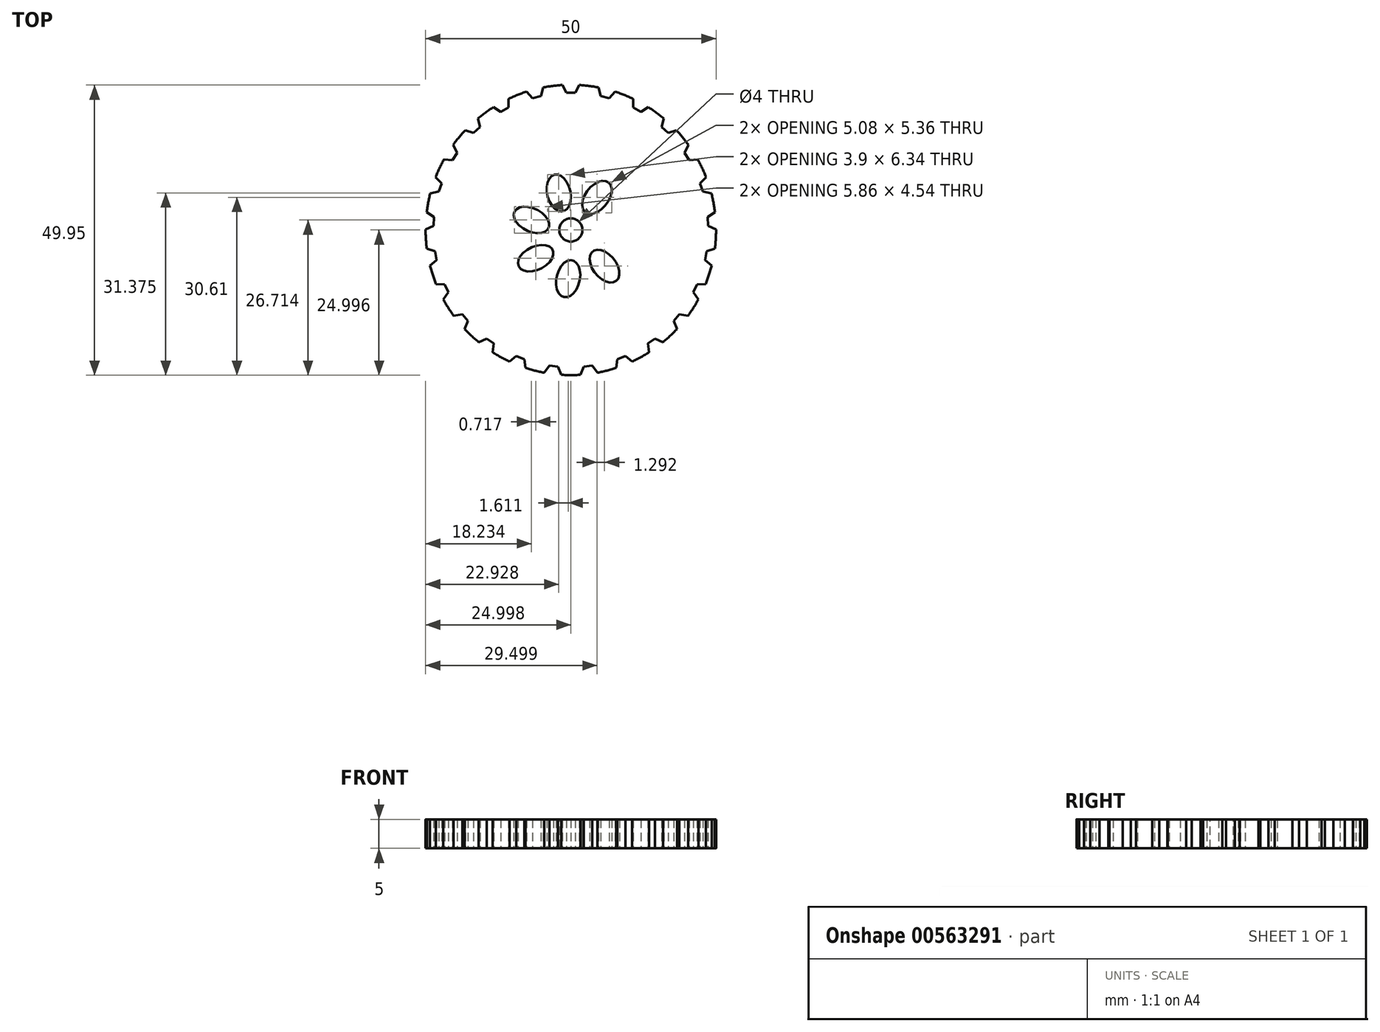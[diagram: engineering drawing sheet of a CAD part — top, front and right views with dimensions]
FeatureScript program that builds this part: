
annotation { "Feature Type Name" : "Feature", "Feature Type Description" : "" }
export const myFeature = defineFeature(function(context is Context, id is Id, definition is map)
    precondition{}
    {
        {
            var Q0;
            Q0=qCreatedBy(makeId("Top.planeOp"),FACE);
            var sketch = newSketch(context, id + "F0", { "sketchPlane" : qUnion([Q0])});
            skArc(sketch, "E0", {"start": v(-18.7, -16.22) * mm, "mid": v(-17.54, -17.4) * mm, "end": v(-16.29, -18.5) * mm});
            skPoint(sketch, "E1.center", {"position": v(0, 0) * mm});
            skArc(sketch, "E2", {"start": v(-8.06, 24.63) * mm, "mid": v(-9.62, 24.07) * mm, "end": v(-11.15, 23.4) * mm});
            skLineSegment(sketch, "E3", {"start": v(-1.9, 25.78) * mm, "end": v(-1.17, 24.47) * mm});
            skLineSegment(sketch, "E4", {"start": v(-1.17, 24.47) * mm, "end": v(0.33, 24.47) * mm});
            skLineSegment(sketch, "E5", {"start": v(0.33, 24.47) * mm, "end": v(1.06, 25.78) * mm});
            skLineSegment(sketch, "E6.1.0", {"start": v(-8.06, 24.63) * mm, "end": v(-7.03, 23.54) * mm});
            skLineSegment(sketch, "E6.1.1", {"start": v(-7.03, 23.54) * mm, "end": v(-5.58, 23.91) * mm});
            skLineSegment(sketch, "E6.1.2", {"start": v(-5.58, 23.91) * mm, "end": v(-5.2, 25.37) * mm});
            skLineSegment(sketch, "E6.2.0", {"start": v(-13.74, 21.98) * mm, "end": v(-12.47, 21.18) * mm});
            skLineSegment(sketch, "E6.2.1", {"start": v(-12.47, 21.18) * mm, "end": v(-11.16, 21.9) * mm});
            skLineSegment(sketch, "E6.2.2", {"start": v(-11.16, 21.9) * mm, "end": v(-11.15, 23.4) * mm});
            skLineSegment(sketch, "E7.2.3.0", {"start": v(-18.58, 18) * mm, "end": v(-17.15, 17.55) * mm});
            skLineSegment(sketch, "E7.3.3.0", {"start": v(-17.15, 17.55) * mm, "end": v(-16.06, 18.58) * mm});
            skLineSegment(sketch, "E7.6.3.0", {"start": v(-16.06, 18.58) * mm, "end": v(-16.43, 20.03) * mm});
            skLineSegment(sketch, "E7.2.4.0", {"start": v(-22.28, 12.95) * mm, "end": v(-20.79, 12.86) * mm});
            skLineSegment(sketch, "E7.3.4.0", {"start": v(-20.79, 12.86) * mm, "end": v(-19.98, 14.13) * mm});
            skLineSegment(sketch, "E7.6.4.0", {"start": v(-19.98, 14.13) * mm, "end": v(-20.7, 15.45) * mm});
            skLineSegment(sketch, "E7.2.5.0", {"start": v(-24.61, 7.13) * mm, "end": v(-23.14, 7.42) * mm});
            skLineSegment(sketch, "E7.3.5.0", {"start": v(-23.14, 7.42) * mm, "end": v(-22.68, 8.85) * mm});
            skLineSegment(sketch, "E7.6.5.0", {"start": v(-22.68, 8.85) * mm, "end": v(-23.7, 9.94) * mm});
            skLineSegment(sketch, "E7.2.6.0", {"start": v(-25.42, 0.92) * mm, "end": v(-24.07, 1.56) * mm});
            skLineSegment(sketch, "E7.3.6.0", {"start": v(-24.07, 1.56) * mm, "end": v(-23.97, 3.06) * mm});
            skLineSegment(sketch, "E7.6.6.0", {"start": v(-23.97, 3.06) * mm, "end": v(-25.24, 3.87) * mm});
            skLineSegment(sketch, "E7.2.7.0", {"start": v(-24.66, -5.3) * mm, "end": v(-23.5, -4.34) * mm});
            skLineSegment(sketch, "E7.3.7.0", {"start": v(-23.5, -4.34) * mm, "end": v(-23.79, -2.87) * mm});
            skLineSegment(sketch, "E7.6.7.0", {"start": v(-23.79, -2.87) * mm, "end": v(-25.21, -2.4) * mm});
            skLineSegment(sketch, "E7.2.8.0", {"start": v(-22.37, -11.14) * mm, "end": v(-21.5, -9.92) * mm});
            skLineSegment(sketch, "E7.3.8.0", {"start": v(-21.5, -9.92) * mm, "end": v(-22.13, -8.56) * mm});
            skLineSegment(sketch, "E7.6.8.0", {"start": v(-22.13, -8.56) * mm, "end": v(-23.63, -8.46) * mm});
            skLineSegment(sketch, "E7.2.9.0", {"start": v(-18.7, -16.22) * mm, "end": v(-18.16, -14.82) * mm});
            skLineSegment(sketch, "E7.3.9.0", {"start": v(-18.16, -14.82) * mm, "end": v(-19.12, -13.67) * mm});
            skLineSegment(sketch, "E7.6.9.0", {"start": v(-19.12, -13.67) * mm, "end": v(-20.6, -13.94) * mm});
            skLineSegment(sketch, "E7.2.10.0", {"start": v(-13.9, -20.23) * mm, "end": v(-13.71, -18.74) * mm});
            skLineSegment(sketch, "E7.3.10.0", {"start": v(-13.71, -18.74) * mm, "end": v(-14.93, -17.86) * mm});
            skLineSegment(sketch, "E7.6.10.0", {"start": v(-14.93, -17.86) * mm, "end": v(-16.29, -18.5) * mm});
            skLineSegment(sketch, "E7.2.11.0", {"start": v(-8.24, -22.92) * mm, "end": v(-8.43, -21.43) * mm});
            skLineSegment(sketch, "E7.3.11.0", {"start": v(-8.43, -21.43) * mm, "end": v(-9.82, -20.88) * mm});
            skLineSegment(sketch, "E7.6.11.0", {"start": v(-9.82, -20.88) * mm, "end": v(-10.98, -21.83) * mm});
            skLineSegment(sketch, "E7.2.12.0", {"start": v(-2.08, -24.12) * mm, "end": v(-2.64, -22.73) * mm});
            skLineSegment(sketch, "E7.3.12.0", {"start": v(-2.64, -22.73) * mm, "end": v(-4.13, -22.54) * mm});
            skLineSegment(sketch, "E7.6.12.0", {"start": v(-4.13, -22.54) * mm, "end": v(-5.01, -23.75) * mm});
            skLineSegment(sketch, "E7.2.13.0", {"start": v(4.17, -23.75) * mm, "end": v(3.29, -22.54) * mm});
            skLineSegment(sketch, "E7.3.13.0", {"start": v(3.29, -22.54) * mm, "end": v(1.8, -22.73) * mm});
            skLineSegment(sketch, "E7.6.13.0", {"start": v(1.8, -22.73) * mm, "end": v(1.24, -24.12) * mm});
            skLineSegment(sketch, "E7.2.14.0", {"start": v(10.14, -21.83) * mm, "end": v(8.98, -20.88) * mm});
            skLineSegment(sketch, "E7.3.14.0", {"start": v(8.98, -20.88) * mm, "end": v(7.59, -21.43) * mm});
            skLineSegment(sketch, "E7.6.14.0", {"start": v(7.59, -21.43) * mm, "end": v(7.4, -22.92) * mm});
            skLineSegment(sketch, "E7.2.15.0", {"start": v(15.44, -18.5) * mm, "end": v(14.08, -17.86) * mm});
            skLineSegment(sketch, "E7.3.15.0", {"start": v(14.08, -17.86) * mm, "end": v(12.87, -18.74) * mm});
            skLineSegment(sketch, "E7.6.15.0", {"start": v(12.87, -18.74) * mm, "end": v(13.05, -20.23) * mm});
            skLineSegment(sketch, "E7.2.16.0", {"start": v(19.75, -13.94) * mm, "end": v(18.27, -13.67) * mm});
            skLineSegment(sketch, "E7.3.16.0", {"start": v(18.27, -13.67) * mm, "end": v(17.32, -14.82) * mm});
            skLineSegment(sketch, "E7.6.16.0", {"start": v(17.32, -14.82) * mm, "end": v(17.87, -16.22) * mm});
            skLineSegment(sketch, "E7.2.17.0", {"start": v(22.79, -8.46) * mm, "end": v(21.3, -8.56) * mm});
            skLineSegment(sketch, "E7.3.17.0", {"start": v(21.3, -8.56) * mm, "end": v(20.65, -9.92) * mm});
            skLineSegment(sketch, "E7.6.17.0", {"start": v(20.65, -9.92) * mm, "end": v(21.53, -11.14) * mm});
            skLineSegment(sketch, "E7.2.18.0", {"start": v(24.37, -2.4) * mm, "end": v(22.94, -2.87) * mm});
            skLineSegment(sketch, "E7.3.18.0", {"start": v(22.94, -2.87) * mm, "end": v(22.66, -4.34) * mm});
            skLineSegment(sketch, "E7.6.18.0", {"start": v(22.66, -4.34) * mm, "end": v(23.82, -5.3) * mm});
            skLineSegment(sketch, "E7.2.19.0", {"start": v(24.4, 3.87) * mm, "end": v(23.13, 3.06) * mm});
            skLineSegment(sketch, "E7.3.19.0", {"start": v(23.13, 3.06) * mm, "end": v(23.22, 1.56) * mm});
            skLineSegment(sketch, "E7.6.19.0", {"start": v(23.22, 1.56) * mm, "end": v(24.58, 0.92) * mm});
            skLineSegment(sketch, "E7.2.20.0", {"start": v(22.86, 9.94) * mm, "end": v(21.83, 8.85) * mm});
            skLineSegment(sketch, "E7.3.20.0", {"start": v(21.83, 8.85) * mm, "end": v(22.3, 7.42) * mm});
            skLineSegment(sketch, "E7.6.20.0", {"start": v(22.3, 7.42) * mm, "end": v(23.77, 7.13) * mm});
            skLineSegment(sketch, "E7.2.21.0", {"start": v(19.86, 15.45) * mm, "end": v(19.14, 14.13) * mm});
            skLineSegment(sketch, "E7.3.21.0", {"start": v(19.14, 14.13) * mm, "end": v(19.94, 12.86) * mm});
            skLineSegment(sketch, "E7.6.21.0", {"start": v(19.94, 12.86) * mm, "end": v(21.44, 12.95) * mm});
            skLineSegment(sketch, "E7.2.22.0", {"start": v(15.59, 20.03) * mm, "end": v(15.22, 18.58) * mm});
            skLineSegment(sketch, "E7.3.22.0", {"start": v(15.22, 18.58) * mm, "end": v(16.31, 17.55) * mm});
            skLineSegment(sketch, "E7.6.22.0", {"start": v(16.31, 17.55) * mm, "end": v(17.74, 18) * mm});
            skLineSegment(sketch, "E7.2.23.0", {"start": v(10.3, 23.4) * mm, "end": v(10.31, 21.9) * mm});
            skLineSegment(sketch, "E7.3.23.0", {"start": v(10.31, 21.9) * mm, "end": v(11.63, 21.18) * mm});
            skLineSegment(sketch, "E7.6.23.0", {"start": v(11.63, 21.18) * mm, "end": v(12.9, 21.98) * mm});
            skLineSegment(sketch, "E7.2.24.0", {"start": v(4.35, 25.37) * mm, "end": v(4.73, 23.91) * mm});
            skLineSegment(sketch, "E7.3.24.0", {"start": v(4.73, 23.91) * mm, "end": v(6.19, 23.54) * mm});
            skLineSegment(sketch, "E7.6.24.0", {"start": v(6.19, 23.54) * mm, "end": v(7.22, 24.63) * mm});
            skArc(sketch, "E8.trimOffspring", {"start": v(-1.9, 25.78) * mm, "mid": v(-3.55, 25.63) * mm, "end": v(-5.2, 25.37) * mm});
            skArc(sketch, "E9.trimOffspring", {"start": v(4.35, 25.37) * mm, "mid": v(2.71, 25.63) * mm, "end": v(1.06, 25.78) * mm});
            skArc(sketch, "E10.trimOffspring", {"start": v(10.3, 23.4) * mm, "mid": v(8.78, 24.07) * mm, "end": v(7.22, 24.63) * mm});
            skArc(sketch, "E11.trimOffspring", {"start": v(15.59, 20.03) * mm, "mid": v(14.27, 21.05) * mm, "end": v(12.9, 21.98) * mm});
            skArc(sketch, "E12.trimOffspring", {"start": v(19.86, 15.45) * mm, "mid": v(18.84, 16.76) * mm, "end": v(17.74, 18) * mm});
            skArc(sketch, "E13.trimOffspring", {"start": v(22.86, 9.94) * mm, "mid": v(22.2, 11.47) * mm, "end": v(21.44, 12.95) * mm});
            skArc(sketch, "E14.trimOffspring", {"start": v(24.4, 3.87) * mm, "mid": v(24.14, 5.51) * mm, "end": v(23.77, 7.13) * mm});
            skArc(sketch, "E15.trimOffspring", {"start": v(24.37, -2.4) * mm, "mid": v(24.53, -0.74) * mm, "end": v(24.58, 0.92) * mm});
            skArc(sketch, "E16.trimOffspring", {"start": v(22.79, -8.46) * mm, "mid": v(23.35, -6.9) * mm, "end": v(23.82, -5.3) * mm});
            skArc(sketch, "E17.trimOffspring", {"start": v(19.75, -13.94) * mm, "mid": v(20.69, -12.57) * mm, "end": v(21.53, -11.14) * mm});
            skArc(sketch, "E18.trimOffspring", {"start": v(15.44, -18.5) * mm, "mid": v(16.7, -17.4) * mm, "end": v(17.87, -16.22) * mm});
            skArc(sketch, "E19.trimOffspring", {"start": v(10.14, -21.83) * mm, "mid": v(11.62, -21.08) * mm, "end": v(13.05, -20.23) * mm});
            skArc(sketch, "E20.trimOffspring", {"start": v(4.17, -23.75) * mm, "mid": v(5.8, -23.39) * mm, "end": v(7.4, -22.92) * mm});
            skArc(sketch, "E21.trimOffspring", {"start": v(-2.08, -24.12) * mm, "mid": v(-0.42, -24.17) * mm, "end": v(1.24, -24.12) * mm});
            skArc(sketch, "E22.trimOffspring", {"start": v(-8.24, -22.92) * mm, "mid": v(-6.64, -23.39) * mm, "end": v(-5.01, -23.75) * mm});
            skArc(sketch, "E23.trimOffspring", {"start": v(-13.9, -20.23) * mm, "mid": v(-12.47, -21.08) * mm, "end": v(-10.98, -21.83) * mm});
            skArc(sketch, "E24.trimOffspring", {"start": v(-22.37, -11.14) * mm, "mid": v(-21.53, -12.57) * mm, "end": v(-20.6, -13.94) * mm});
            skArc(sketch, "E25.trimOffspring", {"start": v(-24.66, -5.3) * mm, "mid": v(-24.2, -6.9) * mm, "end": v(-23.63, -8.46) * mm});
            skArc(sketch, "E26.trimOffspring", {"start": v(-25.42, 0.92) * mm, "mid": v(-25.37, -0.74) * mm, "end": v(-25.21, -2.4) * mm});
            skArc(sketch, "E27.trimOffspring", {"start": v(-24.61, 7.13) * mm, "mid": v(-24.98, 5.51) * mm, "end": v(-25.24, 3.87) * mm});
            skArc(sketch, "E28.trimOffspring", {"start": v(-22.28, 12.95) * mm, "mid": v(-23.04, 11.47) * mm, "end": v(-23.7, 9.94) * mm});
            skArc(sketch, "E29.trimOffspring", {"start": v(-18.58, 18) * mm, "mid": v(-19.68, 16.76) * mm, "end": v(-20.7, 15.45) * mm});
            skArc(sketch, "E30.trimOffspring", {"start": v(-13.74, 21.98) * mm, "mid": v(-15.12, 21.05) * mm, "end": v(-16.43, 20.03) * mm});
            skSolve(sketch);
        }
        {
            var Q0;
            Q0=makeQuery(id+"F0.imprint","IMPRINT",FACE,{"disambiguationData":[TD([[makeQuery(id+"F0.imprint","IMPRINT",EDGE,{"derivedFrom":sQuery(id+"F0.wireOp",EDGE,"E2")}),1.0]])]});
            extrude(context, id + "F1", {"entities" : qUnion([Q0]), "depth" : 5 * mm, "offsetDistance" : 25 * mm});
        }
        {
            var Q0;
            Q0=makeQuery(id+"F1.opExtrude","CAP_FACE",FACE,{"disambiguationData":[OSD([sQuery(id+"F0.wireOp",EDGE,"E2"),sQuery(id+"F0.wireOp",EDGE,"E3"),sQuery(id+"F0.wireOp",EDGE,"E4"),sQuery(id+"F0.wireOp",EDGE,"E5"),sQuery(id+"F0.wireOp",EDGE,"E6.1.0"),sQuery(id+"F0.wireOp",EDGE,"E6.1.1"),sQuery(id+"F0.wireOp",EDGE,"E6.1.2"),sQuery(id+"F0.wireOp",EDGE,"E6.2.0"),sQuery(id+"F0.wireOp",EDGE,"E6.2.1"),sQuery(id+"F0.wireOp",EDGE,"E6.2.2"),sQuery(id+"F0.wireOp",EDGE,"E7.2.3.0"),sQuery(id+"F0.wireOp",EDGE,"E7.3.3.0"),sQuery(id+"F0.wireOp",EDGE,"E7.6.3.0"),sQuery(id+"F0.wireOp",EDGE,"E7.2.4.0"),sQuery(id+"F0.wireOp",EDGE,"E7.3.4.0"),sQuery(id+"F0.wireOp",EDGE,"E7.6.4.0"),sQuery(id+"F0.wireOp",EDGE,"E7.2.5.0"),sQuery(id+"F0.wireOp",EDGE,"E7.3.5.0"),sQuery(id+"F0.wireOp",EDGE,"E7.6.5.0"),sQuery(id+"F0.wireOp",EDGE,"E7.2.6.0"),sQuery(id+"F0.wireOp",EDGE,"E7.3.6.0"),sQuery(id+"F0.wireOp",EDGE,"E7.6.6.0"),sQuery(id+"F0.wireOp",EDGE,"E7.2.7.0"),sQuery(id+"F0.wireOp",EDGE,"E7.3.7.0"),sQuery(id+"F0.wireOp",EDGE,"E7.6.7.0"),sQuery(id+"F0.wireOp",EDGE,"E7.2.8.0"),sQuery(id+"F0.wireOp",EDGE,"E7.3.8.0"),sQuery(id+"F0.wireOp",EDGE,"E7.6.8.0"),sQuery(id+"F0.wireOp",EDGE,"E7.2.9.0"),sQuery(id+"F0.wireOp",EDGE,"E7.3.9.0"),sQuery(id+"F0.wireOp",EDGE,"E7.6.9.0"),sQuery(id+"F0.wireOp",EDGE,"E7.2.10.0"),sQuery(id+"F0.wireOp",EDGE,"E7.3.10.0"),sQuery(id+"F0.wireOp",EDGE,"E7.6.10.0"),sQuery(id+"F0.wireOp",EDGE,"E7.2.11.0"),sQuery(id+"F0.wireOp",EDGE,"E7.3.11.0"),sQuery(id+"F0.wireOp",EDGE,"E7.6.11.0"),sQuery(id+"F0.wireOp",EDGE,"E7.2.12.0"),sQuery(id+"F0.wireOp",EDGE,"E7.3.12.0"),sQuery(id+"F0.wireOp",EDGE,"E7.6.12.0"),sQuery(id+"F0.wireOp",EDGE,"E7.2.13.0"),sQuery(id+"F0.wireOp",EDGE,"E7.3.13.0"),sQuery(id+"F0.wireOp",EDGE,"E7.6.13.0"),sQuery(id+"F0.wireOp",EDGE,"E7.2.14.0"),sQuery(id+"F0.wireOp",EDGE,"E7.3.14.0"),sQuery(id+"F0.wireOp",EDGE,"E7.6.14.0"),sQuery(id+"F0.wireOp",EDGE,"E7.2.15.0"),sQuery(id+"F0.wireOp",EDGE,"E7.3.15.0"),sQuery(id+"F0.wireOp",EDGE,"E7.6.15.0"),sQuery(id+"F0.wireOp",EDGE,"E7.2.16.0"),sQuery(id+"F0.wireOp",EDGE,"E7.3.16.0"),sQuery(id+"F0.wireOp",EDGE,"E7.6.16.0"),sQuery(id+"F0.wireOp",EDGE,"E7.2.17.0"),sQuery(id+"F0.wireOp",EDGE,"E7.3.17.0"),sQuery(id+"F0.wireOp",EDGE,"E7.6.17.0"),sQuery(id+"F0.wireOp",EDGE,"E7.2.18.0"),sQuery(id+"F0.wireOp",EDGE,"E7.3.18.0"),sQuery(id+"F0.wireOp",EDGE,"E7.6.18.0"),sQuery(id+"F0.wireOp",EDGE,"E7.2.19.0"),sQuery(id+"F0.wireOp",EDGE,"E7.3.19.0"),sQuery(id+"F0.wireOp",EDGE,"E7.6.19.0"),sQuery(id+"F0.wireOp",EDGE,"E7.2.20.0"),sQuery(id+"F0.wireOp",EDGE,"E7.3.20.0"),sQuery(id+"F0.wireOp",EDGE,"E7.6.20.0"),sQuery(id+"F0.wireOp",EDGE,"E7.2.21.0"),sQuery(id+"F0.wireOp",EDGE,"E7.3.21.0"),sQuery(id+"F0.wireOp",EDGE,"E7.6.21.0"),sQuery(id+"F0.wireOp",EDGE,"E7.2.22.0"),sQuery(id+"F0.wireOp",EDGE,"E7.3.22.0"),sQuery(id+"F0.wireOp",EDGE,"E7.6.22.0"),sQuery(id+"F0.wireOp",EDGE,"E7.2.23.0"),sQuery(id+"F0.wireOp",EDGE,"E7.3.23.0"),sQuery(id+"F0.wireOp",EDGE,"E7.6.23.0"),sQuery(id+"F0.wireOp",EDGE,"E7.2.24.0"),sQuery(id+"F0.wireOp",EDGE,"E7.3.24.0"),sQuery(id+"F0.wireOp",EDGE,"E7.6.24.0"),sQuery(id+"F0.wireOp",EDGE,"E8.trimOffspring"),sQuery(id+"F0.wireOp",EDGE,"E9.trimOffspring"),sQuery(id+"F0.wireOp",EDGE,"E10.trimOffspring"),sQuery(id+"F0.wireOp",EDGE,"E11.trimOffspring"),sQuery(id+"F0.wireOp",EDGE,"E16.trimOffspring"),sQuery(id+"F0.wireOp",EDGE,"E22.trimOffspring"),sQuery(id+"F0.wireOp",EDGE,"E0"),sQuery(id+"F0.wireOp",EDGE,"E24.trimOffspring"),sQuery(id+"F0.wireOp",EDGE,"E25.trimOffspring"),sQuery(id+"F0.wireOp",EDGE,"E26.trimOffspring"),sQuery(id+"F0.wireOp",EDGE,"E27.trimOffspring"),sQuery(id+"F0.wireOp",EDGE,"E28.trimOffspring"),sQuery(id+"F0.wireOp",EDGE,"E29.trimOffspring"),sQuery(id+"F0.wireOp",EDGE,"E30.trimOffspring"),sQuery(id+"F0.wireOp",EDGE,"E17.trimOffspring"),sQuery(id+"F0.wireOp",EDGE,"E18.trimOffspring"),sQuery(id+"F0.wireOp",EDGE,"E19.trimOffspring"),sQuery(id+"F0.wireOp",EDGE,"E20.trimOffspring"),sQuery(id+"F0.wireOp",EDGE,"E21.trimOffspring"),sQuery(id+"F0.wireOp",EDGE,"E23.trimOffspring"),sQuery(id+"F0.wireOp",EDGE,"E12.trimOffspring"),sQuery(id+"F0.wireOp",EDGE,"E13.trimOffspring"),sQuery(id+"F0.wireOp",EDGE,"E14.trimOffspring"),sQuery(id+"F0.wireOp",EDGE,"E15.trimOffspring")])],"isStart":false});
            var sketch = newSketch(context, id + "F2", { "sketchPlane" : qUnion([Q0])});
            skCircle(sketch, "E31", {"center": v(-0.42, 0.83) * mm, "radius": 12.5 * mm});
            skLineSegment(sketch, "E32", {"start": v(-0.42, 0.83) * mm, "end": v(7.58, 0.83) * mm});
            skEllipse(sketch, "E33", {"center": v(7.58, 0.83) * mm, "majorRadius": 3.25 * mm, "minorRadius": 2 * mm, "majorAxis": v(1, 0)});
            skEllipse(sketch, "E34.1.0", {"center": v(7.58, 0.83) * mm, "majorRadius": 3.25 * mm, "minorRadius": 2 * mm, "majorAxis": v(1, 0)});
            skEllipse(sketch, "E34.2.0", {"center": v(7.58, 0.83) * mm, "majorRadius": 3.25 * mm, "minorRadius": 2 * mm, "majorAxis": v(1, 0)});
            skEllipse(sketch, "E34.3.0", {"center": v(7.58, 0.83) * mm, "majorRadius": 3.25 * mm, "minorRadius": 2 * mm, "majorAxis": v(1, 0)});
            skEllipse(sketch, "E34.4.0", {"center": v(7.58, 0.83) * mm, "majorRadius": 3.25 * mm, "minorRadius": 2 * mm, "majorAxis": v(1, 0)});
            skEllipse(sketch, "E34.5.0", {"center": v(7.58, 0.83) * mm, "majorRadius": 3.25 * mm, "minorRadius": 2 * mm, "majorAxis": v(1, 0)});
            skEllipse(sketch, "E34.6.0", {"center": v(7.58, 0.83) * mm, "majorRadius": 3.25 * mm, "minorRadius": 2 * mm, "majorAxis": v(1, 0)});
            skEllipse(sketch, "E34.7.0", {"center": v(7.58, 0.83) * mm, "majorRadius": 3.25 * mm, "minorRadius": 2 * mm, "majorAxis": v(1, 0)});
            skPoint(sketch, "E34.center", {"position": v(0, 0) * mm});
            skEllipse(sketch, "E35.1.0", {"center": v(7.58, 0.83) * mm, "majorRadius": 3.25 * mm, "minorRadius": 2 * mm, "majorAxis": v(1, 0)});
            skEllipse(sketch, "E35.2.0", {"center": v(7.58, 0.83) * mm, "majorRadius": 3.25 * mm, "minorRadius": 2 * mm, "majorAxis": v(1, 0)});
            skEllipse(sketch, "E35.3.0", {"center": v(7.58, 0.83) * mm, "majorRadius": 3.25 * mm, "minorRadius": 2 * mm, "majorAxis": v(1, 0)});
            skEllipse(sketch, "E35.4.0", {"center": v(7.58, 0.83) * mm, "majorRadius": 3.25 * mm, "minorRadius": 2 * mm, "majorAxis": v(1, 0)});
            skEllipse(sketch, "E35.5.0", {"center": v(7.58, 0.83) * mm, "majorRadius": 3.25 * mm, "minorRadius": 2 * mm, "majorAxis": v(1, 0)});
            skEllipse(sketch, "E35.6.0", {"center": v(7.58, 0.83) * mm, "majorRadius": 3.25 * mm, "minorRadius": 2 * mm, "majorAxis": v(1, 0)});
            skEllipse(sketch, "E35.7.0", {"center": v(7.58, 0.83) * mm, "majorRadius": 3.25 * mm, "minorRadius": 2 * mm, "majorAxis": v(1, 0)});
            skEllipse(sketch, "E36.1.0", {"center": v(7.58, 0.83) * mm, "majorRadius": 3.25 * mm, "minorRadius": 2 * mm, "majorAxis": v(1, 0)});
            skEllipse(sketch, "E36.2.0", {"center": v(7.58, 0.83) * mm, "majorRadius": 3.25 * mm, "minorRadius": 2 * mm, "majorAxis": v(1, 0)});
            skEllipse(sketch, "E36.3.0", {"center": v(7.58, 0.83) * mm, "majorRadius": 3.25 * mm, "minorRadius": 2 * mm, "majorAxis": v(1, 0)});
            skEllipse(sketch, "E36.4.0", {"center": v(7.58, 0.83) * mm, "majorRadius": 3.25 * mm, "minorRadius": 2 * mm, "majorAxis": v(1, 0)});
            skEllipse(sketch, "E36.5.0", {"center": v(7.58, 0.83) * mm, "majorRadius": 3.25 * mm, "minorRadius": 2 * mm, "majorAxis": v(1, 0)});
            skEllipse(sketch, "E36.6.0", {"center": v(7.58, 0.83) * mm, "majorRadius": 3.25 * mm, "minorRadius": 2 * mm, "majorAxis": v(1, 0)});
            skEllipse(sketch, "E36.7.0", {"center": v(7.58, 0.83) * mm, "majorRadius": 3.25 * mm, "minorRadius": 2 * mm, "majorAxis": v(1, 0)});
            skEllipse(sketch, "E37.1.0", {"center": v(4.08, 6.44) * mm, "majorRadius": 3.25 * mm, "minorRadius": 2 * mm, "majorAxis": v(0.62, 0.78)});
            skEllipse(sketch, "E37.2.0", {"center": v(-2.5, 7.2) * mm, "majorRadius": 3.25 * mm, "minorRadius": 2 * mm, "majorAxis": v(-0.22, 0.97)});
            skEllipse(sketch, "E37.3.0", {"center": v(-7.19, 2.54) * mm, "majorRadius": 3.25 * mm, "minorRadius": 2 * mm, "majorAxis": v(-0.9, 0.43)});
            skEllipse(sketch, "E37.4.0", {"center": v(-6.47, -4.03) * mm, "majorRadius": 3.25 * mm, "minorRadius": 2 * mm, "majorAxis": v(-0.9, -0.43)});
            skEllipse(sketch, "E37.5.0", {"center": v(-0.88, -7.57) * mm, "majorRadius": 3.25 * mm, "minorRadius": 2 * mm, "majorAxis": v(-0.22, -0.97)});
            skEllipse(sketch, "E37.6.0", {"center": v(5.37, -5.41) * mm, "majorRadius": 3.25 * mm, "minorRadius": 2 * mm, "majorAxis": v(0.62, -0.78)});
            skCircle(sketch, "E38", {"center": v(-0.42, 0.83) * mm, "radius": 2 * mm});
            skSolve(sketch);
        }
        {
            var Q0;
            Q0=makeQuery(id+"F2.imprint","IMPRINT",FACE,{"disambiguationData":[TD([[makeQuery(id+"F2.imprint","IMPRINT",EDGE,{"derivedFrom":sQuery(id+"F2.wireOp",EDGE,"E36.7.0")}),1.0]])]});
            var Q1;
            Q1=makeQuery(id+"F2.imprint","IMPRINT",FACE,{"disambiguationData":[TD([[makeQuery(id+"F2.imprint","IMPRINT",EDGE,{"derivedFrom":sQuery(id+"F2.wireOp",EDGE,"E37.1.0")}),1.0]])]});
            var Q2;
            Q2=makeQuery(id+"F2.imprint","IMPRINT",FACE,{"disambiguationData":[TD([[makeQuery(id+"F2.imprint","IMPRINT",EDGE,{"derivedFrom":sQuery(id+"F2.wireOp",EDGE,"E37.2.0")}),1.0]])]});
            var Q3;
            Q3=makeQuery(id+"F2.imprint","IMPRINT",FACE,{"disambiguationData":[TD([[makeQuery(id+"F2.imprint","IMPRINT",EDGE,{"derivedFrom":sQuery(id+"F2.wireOp",EDGE,"E37.3.0")}),1.0]])]});
            var Q4;
            Q4=makeQuery(id+"F2.imprint","IMPRINT",FACE,{"disambiguationData":[TD([[makeQuery(id+"F2.imprint","IMPRINT",EDGE,{"derivedFrom":sQuery(id+"F2.wireOp",EDGE,"E37.4.0")}),1.0]])]});
            var Q5;
            Q5=makeQuery(id+"F2.imprint","IMPRINT",FACE,{"disambiguationData":[TD([[makeQuery(id+"F2.imprint","IMPRINT",EDGE,{"derivedFrom":sQuery(id+"F2.wireOp",EDGE,"E37.5.0")}),1.0]])]});
            var Q6;
            Q6=makeQuery(id+"F2.imprint","IMPRINT",FACE,{"disambiguationData":[TD([[makeQuery(id+"F2.imprint","IMPRINT",EDGE,{"derivedFrom":sQuery(id+"F2.wireOp",EDGE,"E37.6.0")}),1.0]])]});
            extrude(context, id + "F3", {"entities" : qUnion([Q0, Q1, Q2, Q3, Q4, Q5, Q6]), "operationType" : NewBodyOperationType.REMOVE, "oppositeDirection" : true, "depth" : 25 * mm, "offsetDistance" : 25 * mm});
        }
        {
            var Q0;
            Q0=makeQuery(id+"F1.opExtrude","CAP_FACE",FACE,{"disambiguationData":[OSD([sQuery(id+"F0.wireOp",EDGE,"E2"),sQuery(id+"F0.wireOp",EDGE,"E3"),sQuery(id+"F0.wireOp",EDGE,"E4"),sQuery(id+"F0.wireOp",EDGE,"E5"),sQuery(id+"F0.wireOp",EDGE,"E6.1.0"),sQuery(id+"F0.wireOp",EDGE,"E6.1.1"),sQuery(id+"F0.wireOp",EDGE,"E6.1.2"),sQuery(id+"F0.wireOp",EDGE,"E6.2.0"),sQuery(id+"F0.wireOp",EDGE,"E6.2.1"),sQuery(id+"F0.wireOp",EDGE,"E6.2.2"),sQuery(id+"F0.wireOp",EDGE,"E7.2.3.0"),sQuery(id+"F0.wireOp",EDGE,"E7.3.3.0"),sQuery(id+"F0.wireOp",EDGE,"E7.6.3.0"),sQuery(id+"F0.wireOp",EDGE,"E7.2.4.0"),sQuery(id+"F0.wireOp",EDGE,"E7.3.4.0"),sQuery(id+"F0.wireOp",EDGE,"E7.6.4.0"),sQuery(id+"F0.wireOp",EDGE,"E7.2.5.0"),sQuery(id+"F0.wireOp",EDGE,"E7.3.5.0"),sQuery(id+"F0.wireOp",EDGE,"E7.6.5.0"),sQuery(id+"F0.wireOp",EDGE,"E7.2.6.0"),sQuery(id+"F0.wireOp",EDGE,"E7.3.6.0"),sQuery(id+"F0.wireOp",EDGE,"E7.6.6.0"),sQuery(id+"F0.wireOp",EDGE,"E7.2.7.0"),sQuery(id+"F0.wireOp",EDGE,"E7.3.7.0"),sQuery(id+"F0.wireOp",EDGE,"E7.6.7.0"),sQuery(id+"F0.wireOp",EDGE,"E7.2.8.0"),sQuery(id+"F0.wireOp",EDGE,"E7.3.8.0"),sQuery(id+"F0.wireOp",EDGE,"E7.6.8.0"),sQuery(id+"F0.wireOp",EDGE,"E7.2.9.0"),sQuery(id+"F0.wireOp",EDGE,"E7.3.9.0"),sQuery(id+"F0.wireOp",EDGE,"E7.6.9.0"),sQuery(id+"F0.wireOp",EDGE,"E7.2.10.0"),sQuery(id+"F0.wireOp",EDGE,"E7.3.10.0"),sQuery(id+"F0.wireOp",EDGE,"E7.6.10.0"),sQuery(id+"F0.wireOp",EDGE,"E7.2.11.0"),sQuery(id+"F0.wireOp",EDGE,"E7.3.11.0"),sQuery(id+"F0.wireOp",EDGE,"E7.6.11.0"),sQuery(id+"F0.wireOp",EDGE,"E7.2.12.0"),sQuery(id+"F0.wireOp",EDGE,"E7.3.12.0"),sQuery(id+"F0.wireOp",EDGE,"E7.6.12.0"),sQuery(id+"F0.wireOp",EDGE,"E7.2.13.0"),sQuery(id+"F0.wireOp",EDGE,"E7.3.13.0"),sQuery(id+"F0.wireOp",EDGE,"E7.6.13.0"),sQuery(id+"F0.wireOp",EDGE,"E7.2.14.0"),sQuery(id+"F0.wireOp",EDGE,"E7.3.14.0"),sQuery(id+"F0.wireOp",EDGE,"E7.6.14.0"),sQuery(id+"F0.wireOp",EDGE,"E7.2.15.0"),sQuery(id+"F0.wireOp",EDGE,"E7.3.15.0"),sQuery(id+"F0.wireOp",EDGE,"E7.6.15.0"),sQuery(id+"F0.wireOp",EDGE,"E7.2.16.0"),sQuery(id+"F0.wireOp",EDGE,"E7.3.16.0"),sQuery(id+"F0.wireOp",EDGE,"E7.6.16.0"),sQuery(id+"F0.wireOp",EDGE,"E7.2.17.0"),sQuery(id+"F0.wireOp",EDGE,"E7.3.17.0"),sQuery(id+"F0.wireOp",EDGE,"E7.6.17.0"),sQuery(id+"F0.wireOp",EDGE,"E7.2.18.0"),sQuery(id+"F0.wireOp",EDGE,"E7.3.18.0"),sQuery(id+"F0.wireOp",EDGE,"E7.6.18.0"),sQuery(id+"F0.wireOp",EDGE,"E7.2.19.0"),sQuery(id+"F0.wireOp",EDGE,"E7.3.19.0"),sQuery(id+"F0.wireOp",EDGE,"E7.6.19.0"),sQuery(id+"F0.wireOp",EDGE,"E7.2.20.0"),sQuery(id+"F0.wireOp",EDGE,"E7.3.20.0"),sQuery(id+"F0.wireOp",EDGE,"E7.6.20.0"),sQuery(id+"F0.wireOp",EDGE,"E7.2.21.0"),sQuery(id+"F0.wireOp",EDGE,"E7.3.21.0"),sQuery(id+"F0.wireOp",EDGE,"E7.6.21.0"),sQuery(id+"F0.wireOp",EDGE,"E7.2.22.0"),sQuery(id+"F0.wireOp",EDGE,"E7.3.22.0"),sQuery(id+"F0.wireOp",EDGE,"E7.6.22.0"),sQuery(id+"F0.wireOp",EDGE,"E7.2.23.0"),sQuery(id+"F0.wireOp",EDGE,"E7.3.23.0"),sQuery(id+"F0.wireOp",EDGE,"E7.6.23.0"),sQuery(id+"F0.wireOp",EDGE,"E7.2.24.0"),sQuery(id+"F0.wireOp",EDGE,"E7.3.24.0"),sQuery(id+"F0.wireOp",EDGE,"E7.6.24.0"),sQuery(id+"F0.wireOp",EDGE,"E8.trimOffspring"),sQuery(id+"F0.wireOp",EDGE,"E9.trimOffspring"),sQuery(id+"F0.wireOp",EDGE,"E10.trimOffspring"),sQuery(id+"F0.wireOp",EDGE,"E11.trimOffspring"),sQuery(id+"F0.wireOp",EDGE,"E16.trimOffspring"),sQuery(id+"F0.wireOp",EDGE,"E22.trimOffspring"),sQuery(id+"F0.wireOp",EDGE,"E0"),sQuery(id+"F0.wireOp",EDGE,"E24.trimOffspring"),sQuery(id+"F0.wireOp",EDGE,"E25.trimOffspring"),sQuery(id+"F0.wireOp",EDGE,"E26.trimOffspring"),sQuery(id+"F0.wireOp",EDGE,"E27.trimOffspring"),sQuery(id+"F0.wireOp",EDGE,"E28.trimOffspring"),sQuery(id+"F0.wireOp",EDGE,"E29.trimOffspring"),sQuery(id+"F0.wireOp",EDGE,"E30.trimOffspring"),sQuery(id+"F0.wireOp",EDGE,"E17.trimOffspring"),sQuery(id+"F0.wireOp",EDGE,"E18.trimOffspring"),sQuery(id+"F0.wireOp",EDGE,"E19.trimOffspring"),sQuery(id+"F0.wireOp",EDGE,"E20.trimOffspring"),sQuery(id+"F0.wireOp",EDGE,"E21.trimOffspring"),sQuery(id+"F0.wireOp",EDGE,"E23.trimOffspring"),sQuery(id+"F0.wireOp",EDGE,"E12.trimOffspring"),sQuery(id+"F0.wireOp",EDGE,"E13.trimOffspring"),sQuery(id+"F0.wireOp",EDGE,"E14.trimOffspring"),sQuery(id+"F0.wireOp",EDGE,"E15.trimOffspring")])],"isStart":false});
            var sketch = newSketch(context, id + "F4", { "sketchPlane" : qUnion([Q0])});
            skCircle(sketch, "E39", {"center": v(-0.42, 0.83) * mm, "radius": 2 * mm});
            skSolve(sketch);
        }
        {
            var Q0;
            Q0 = qSketchRegion(id + "F4", true);
            extrude(context, id + "F5", {"entities" : qUnion([Q0]), "operationType" : NewBodyOperationType.REMOVE, "oppositeDirection" : true, "depth" : 25 * mm, "offsetDistance" : 25 * mm});
        }
    });
